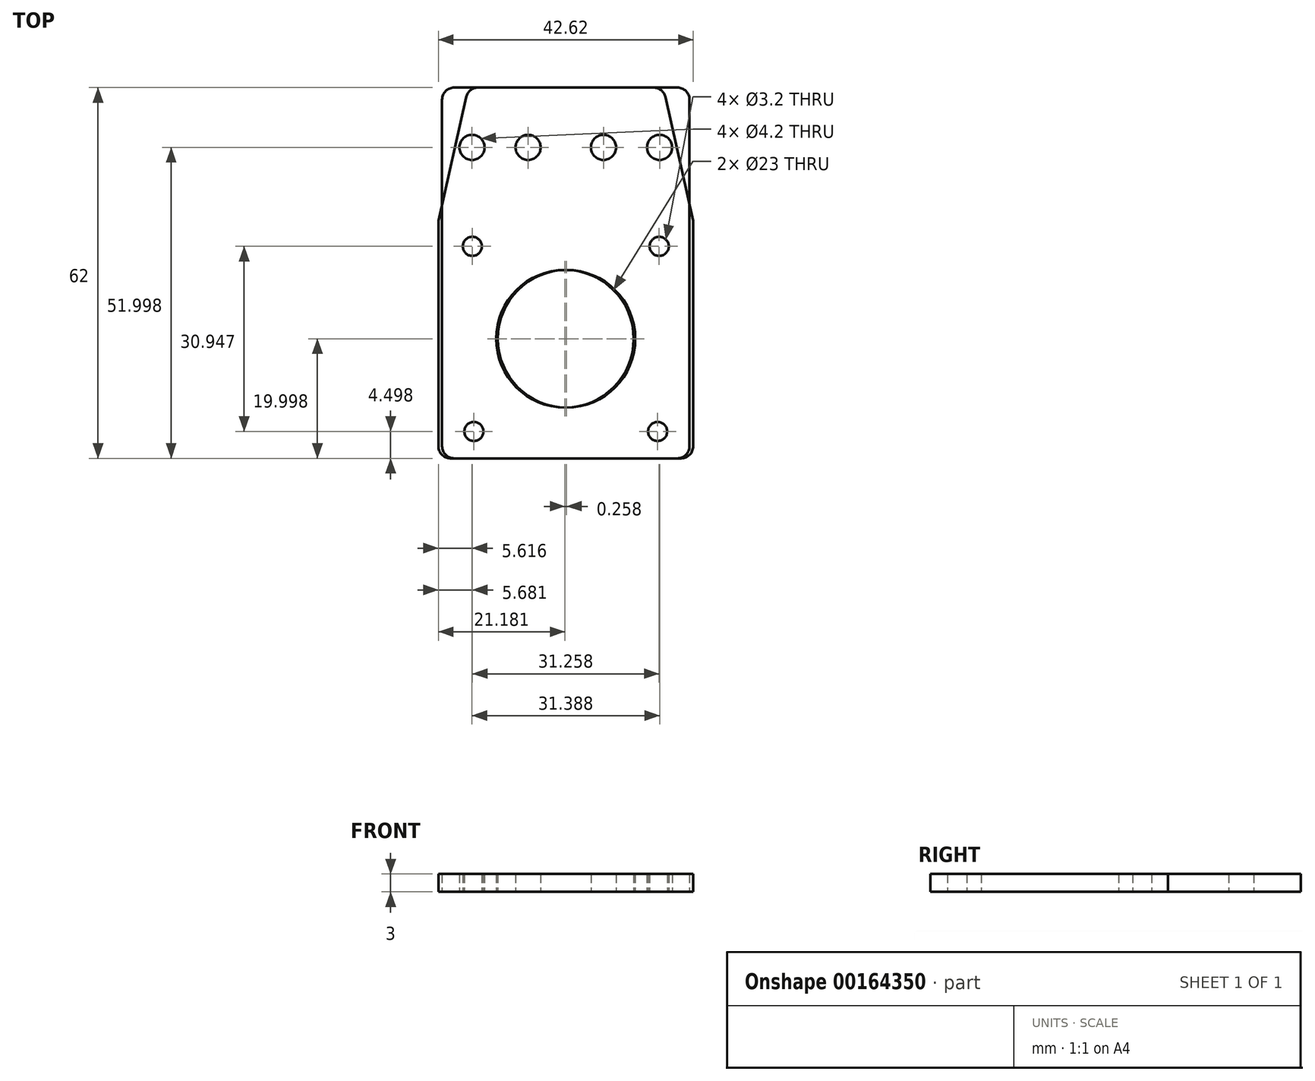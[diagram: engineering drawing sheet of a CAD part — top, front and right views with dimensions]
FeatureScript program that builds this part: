
annotation { "Feature Type Name" : "Feature", "Feature Type Description" : "" }
export const myFeature = defineFeature(function(context is Context, id is Id, definition is map)
    precondition{}
    {
        {
            var Q0;
            Q0=qCreatedBy(makeId("Top.planeOp"),FACE);
            var sketch = newSketch(context, id + "F0", { "sketchPlane" : qUnion([Q0])});
            skCircle(sketch, "E0", {"center": v(-0.13, -28.42) * mm, "radius": 11.5 * mm});
            skCircle(sketch, "E1", {"center": v(15.37, -43.92) * mm, "radius": 1.6 * mm});
            skCircle(sketch, "E2", {"center": v(-15.63, -12.97) * mm, "radius": 1.6 * mm});
            skLineSegment(sketch, "E3.bottom", {"start": v(-18.7, 13.58) * mm, "end": v(14.7, 13.58) * mm});
            skLineSegment(sketch, "E3.top", {"start": v(-18.7, -48.42) * mm, "end": v(19.3, -48.42) * mm});
            skLineSegment(sketch, "E3.left", {"start": v(-20.7, 11.58) * mm, "end": v(-20.7, -46.42) * mm});
            skLineSegment(sketch, "E3.right", {"start": v(21.3, -8.68) * mm, "end": v(21.3, -46.42) * mm});
            skCircle(sketch, "E4", {"center": v(-15.7, 3.58) * mm, "radius": 2.1 * mm});
            skCircle(sketch, "E5", {"center": v(6.3, 3.58) * mm, "radius": 2.1 * mm});
            skPoint(sketch, "E6.visualSharp", {"position": v(-20.7, 13.58) * mm});
            skArc(sketch, "E6.filletArc", {"start": v(-18.7, 13.58) * mm, "mid": v(-20.1, 13) * mm, "end": v(-20.7, 11.58) * mm});
            skPoint(sketch, "E7.visualSharp", {"position": v(21.3, -48.42) * mm});
            skArc(sketch, "E7.filletArc", {"start": v(19.3, -48.42) * mm, "mid": v(20.72, -47.84) * mm, "end": v(21.3, -46.42) * mm});
            skPoint(sketch, "E8.visualSharp", {"position": v(-20.7, -48.42) * mm});
            skArc(sketch, "E8.filletArc", {"start": v(-20.7, -46.42) * mm, "mid": v(-20.1, -47.84) * mm, "end": v(-18.7, -48.42) * mm});
            skLineSegment(sketch, "E9", {"start": v(16.66, 12.02) * mm, "end": v(21.3, -8.68) * mm});
            skPoint(sketch, "E10.visualSharp", {"position": v(16.3, 13.58) * mm});
            skArc(sketch, "E10.filletArc", {"start": v(16.66, 12.02) * mm, "mid": v(15.96, 13.14) * mm, "end": v(14.7, 13.58) * mm});
            skSolve(sketch);
        }
        {
            var Q0;
            Q0 = qSketchRegion(id + "F0", true);
            extrude(context, id + "F1", {"entities" : qUnion([Q0]), "depth" : 3 * mm});
        }
        {
            var Q0;
            Q0=makeQuery(id+"F1.opExtrude","SWEPT_BODY",BODY,{"disambiguationData":[OSD([sQuery(id+"F0.wireOp",EDGE,"E0"),sQuery(id+"F0.wireOp",EDGE,"E1"),sQuery(id+"F0.wireOp",EDGE,"E2"),sQuery(id+"F0.wireOp",EDGE,"E3.bottom"),sQuery(id+"F0.wireOp",EDGE,"E3.top"),sQuery(id+"F0.wireOp",EDGE,"E3.left"),sQuery(id+"F0.wireOp",EDGE,"E3.right"),sQuery(id+"F0.wireOp",EDGE,"E4"),sQuery(id+"F0.wireOp",EDGE,"E5"),sQuery(id+"F0.wireOp",EDGE,"E6.filletArc"),sQuery(id+"F0.wireOp",EDGE,"E7.filletArc"),sQuery(id+"F0.wireOp",EDGE,"E8.filletArc"),sQuery(id+"F0.wireOp",EDGE,"E9")])]});
            var Q1;
            Q1=qCreatedBy(makeId("Right.planeOp"),FACE);
            mirror(context, id + "F2", {"entities" : qUnion([Q0]), "mirrorPlane" : qUnion([Q1])});
        }
    });
